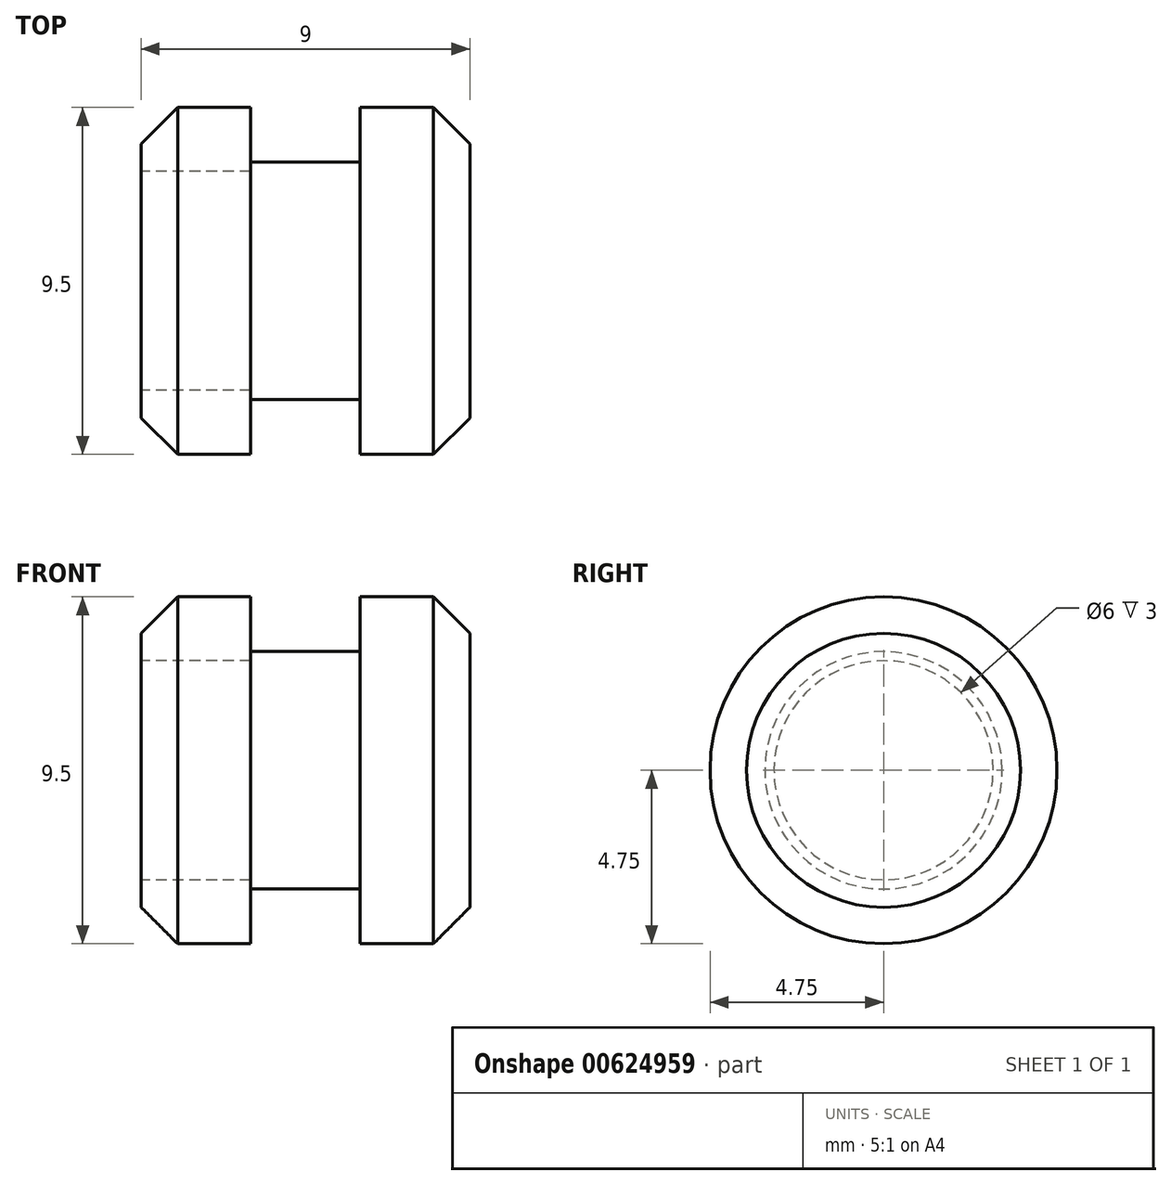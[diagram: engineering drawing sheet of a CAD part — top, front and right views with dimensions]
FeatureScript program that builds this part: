
annotation { "Feature Type Name" : "Feature", "Feature Type Description" : "" }
export const myFeature = defineFeature(function(context is Context, id is Id, definition is map)
    precondition{}
    {
        {
            var Q0;
            Q0=qCreatedBy(makeId("Front.planeOp"),FACE);
            var sketch = newSketch(context, id + "F0", { "sketchPlane" : qUnion([Q0])});
            skLineSegment(sketch, "E0", {"start": v(0, 4.75) * mm, "end": v(3, 4.75) * mm});
            skLineSegment(sketch, "E1", {"start": v(3, 4.75) * mm, "end": v(3, 3.25) * mm});
            skLineSegment(sketch, "E2", {"start": v(3, 3.25) * mm, "end": v(6, 3.25) * mm});
            skLineSegment(sketch, "E3", {"start": v(6, 3.25) * mm, "end": v(6, 4.75) * mm});
            skLineSegment(sketch, "E4", {"start": v(6, 4.75) * mm, "end": v(9, 4.75) * mm});
            skLineSegment(sketch, "E5", {"start": v(0, 4.75) * mm, "end": v(0, 0) * mm});
            skLineSegment(sketch, "E6", {"start": v(9, 4.75) * mm, "end": v(9, 0) * mm});
            skLineSegment(sketch, "E7", {"start": v(0, 0) * mm, "end": v(9, 0) * mm});
            skSolve(sketch);
        }
        {
            var Q0;
            Q0 = qSketchRegion(id + "F0", true);
            var Q1;
            Q1=sQuery(id+"F0.wireOp",EDGE,"E7");
            revolve(context, id + "F1", {"entities" : qUnion([Q0]), "axis" : qUnion([Q1]), "revolveType" : RevolveType.FULL});
        }
        {
            var Q0;
            Q0=makeQuery(id+"F1.opRevolve","SWEPT_EDGE",EDGE,{"disambiguationData":[OSD([sQuery(id+"F0.wireOp",EDGE,"E0"),sQuery(id+"F0.wireOp",EDGE,"E5")])]});
            var Q1;
            Q1=makeQuery(id+"F1.opRevolve","SWEPT_EDGE",EDGE,{"disambiguationData":[OSD([sQuery(id+"F0.wireOp",EDGE,"E4"),sQuery(id+"F0.wireOp",EDGE,"E6")])]});
            chamfer(context, id + "F2", {"entities" : qUnion([Q0, Q1]), "width" : 1 * mm, "tangentPropagation" : true});
        }
        {
            var Q0;
            Q0=makeQuery(id+"F1.opRevolve","SWEPT_FACE",FACE,{"disambiguationData":[OSD([sQuery(id+"F0.wireOp",EDGE,"E5")])]});
            var sketch = newSketch(context, id + "F3", { "sketchPlane" : qUnion([Q0])});
            skCircle(sketch, "E8", {"center": v(0, 0) * mm, "radius": 3 * mm});
            skSolve(sketch);
        }
        {
            var Q0;
            Q0=makeQuery(id+"F3.imprint","IMPRINT",FACE,{"disambiguationData":[TD([[makeQuery(id+"F3.imprint","IMPRINT",EDGE,{"derivedFrom":sQuery(id+"F3.wireOp",EDGE,"E8")}),1.0]])]});
            extrude(context, id + "F4", {"entities" : qUnion([Q0]), "operationType" : NewBodyOperationType.REMOVE, "oppositeDirection" : true, "depth" : 3 * mm, "offsetDistance" : 25 * mm});
        }
    });
